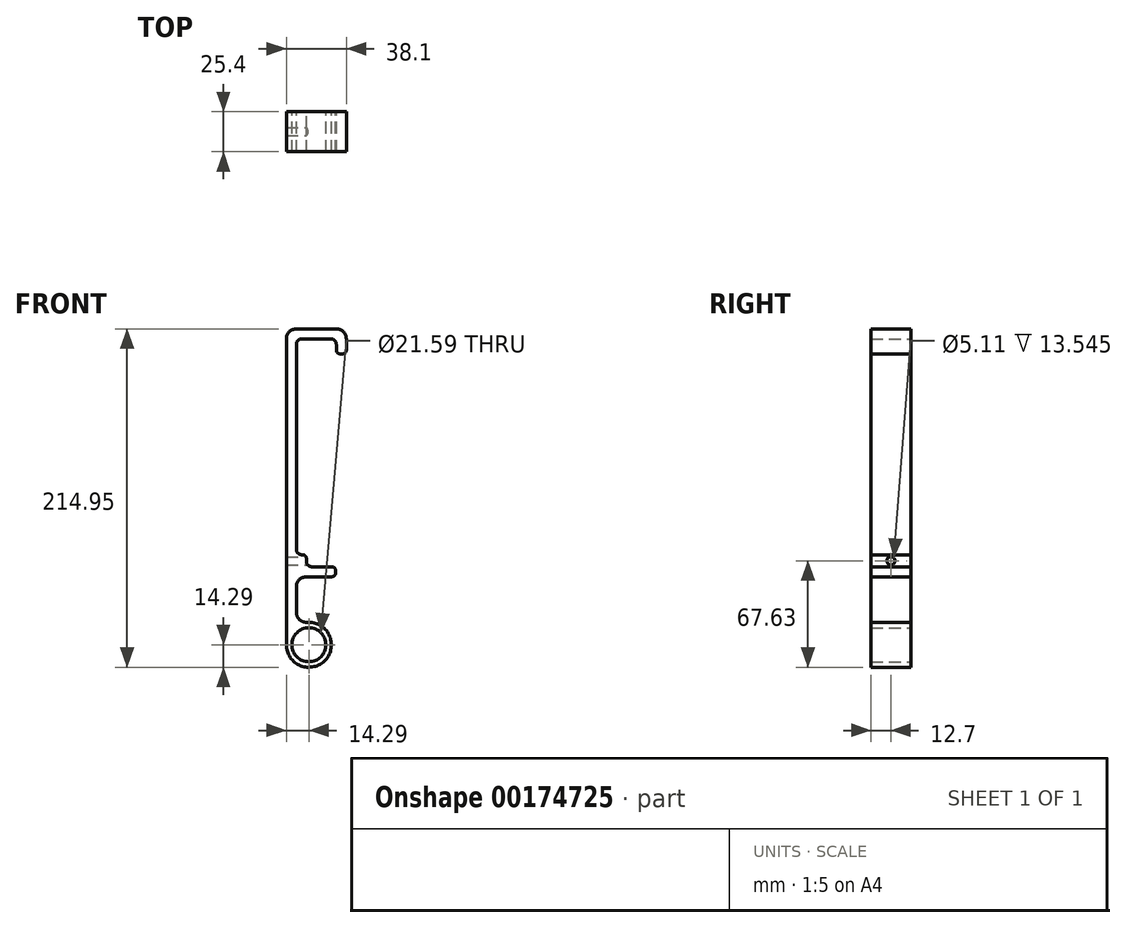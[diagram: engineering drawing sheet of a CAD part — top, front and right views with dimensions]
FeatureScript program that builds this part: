
annotation { "Feature Type Name" : "Feature", "Feature Type Description" : "" }
export const myFeature = defineFeature(function(context is Context, id is Id, definition is map)
    precondition{}
    {
        {
            var Q0;
            Q0=qCreatedBy(makeId("Front.planeOp"),FACE);
            var sketch = newSketch(context, id + "F0", { "sketchPlane" : qUnion([Q0])});
            skCircle(sketch, "E0", {"center": v(0, 0) * mm, "radius": 10.8 * mm});
            skArc(sketch, "E1", {"start": v(-14.29, 0) * mm, "mid": v(12.6, -6.74) * mm, "end": v(-7.94, 11.88) * mm});
            skLineSegment(sketch, "E2", {"start": v(-14.29, 0) * mm, "end": v(-14.29, 200.66) * mm});
            skLineSegment(sketch, "E3", {"start": v(23.81, 200.66) * mm, "end": v(23.81, 184.79) * mm});
            skLineSegment(sketch, "E4", {"start": v(23.81, 184.79) * mm, "end": v(17.46, 184.79) * mm});
            skLineSegment(sketch, "E5", {"start": v(17.46, 184.79) * mm, "end": v(17.46, 194.31) * mm});
            skLineSegment(sketch, "E6", {"start": v(17.46, 194.31) * mm, "end": v(-7.94, 194.31) * mm});
            skLineSegment(sketch, "E7", {"start": v(-7.94, 194.31) * mm, "end": v(-7.94, 57.15) * mm});
            skLineSegment(sketch, "E8", {"start": v(-14.29, 200.66) * mm, "end": v(23.81, 200.66) * mm});
            skLineSegment(sketch, "E9", {"start": v(-1.59, 49.53) * mm, "end": v(16.95, 49.53) * mm});
            skLineSegment(sketch, "E10", {"start": v(16.95, 49.53) * mm, "end": v(16.95, 43.18) * mm});
            skLineSegment(sketch, "E11", {"start": v(16.95, 43.18) * mm, "end": v(-7.94, 43.18) * mm});
            skLineSegment(sketch, "E12.trimOffspring", {"start": v(-7.94, 43.18) * mm, "end": v(-7.94, 11.88) * mm});
            skLineSegment(sketch, "E13", {"start": v(-1.59, 49.53) * mm, "end": v(-1.59, 57.15) * mm});
            skLineSegment(sketch, "E14", {"start": v(-1.59, 57.15) * mm, "end": v(-7.94, 57.15) * mm});
            skSolve(sketch);
        }
        {
            var Q0;
            Q0 = qSketchRegion(id + "F0", true);
            extrude(context, id + "F1", {"entities" : qUnion([Q0]), "depth" : 25.4 * mm});
        }
        {
            var Q0;
            Q0=makeQuery(id+"F1.opExtrude","SWEPT_EDGE",EDGE,{"disambiguationData":[OSD([sQuery(id+"F0.wireOp",EDGE,"E10"),sQuery(id+"F0.wireOp",EDGE,"E11")])]});
            var Q1;
            Q1=makeQuery(id+"F1.opExtrude","SWEPT_EDGE",EDGE,{"disambiguationData":[OSD([sQuery(id+"F0.wireOp",EDGE,"E9"),sQuery(id+"F0.wireOp",EDGE,"E10")])]});
            var Q2;
            Q2=makeQuery(id+"F1.opExtrude","SWEPT_EDGE",EDGE,{"disambiguationData":[OSD([sQuery(id+"F0.wireOp",EDGE,"E3"),sQuery(id+"F0.wireOp",EDGE,"E4")])]});
            var Q3;
            Q3=makeQuery(id+"F1.opExtrude","SWEPT_EDGE",EDGE,{"disambiguationData":[OSD([sQuery(id+"F0.wireOp",EDGE,"E4"),sQuery(id+"F0.wireOp",EDGE,"E5")])]});
            var Q4;
            Q4=makeQuery(id+"F1.opExtrude","SWEPT_EDGE",EDGE,{"disambiguationData":[OSD([sQuery(id+"F0.wireOp",EDGE,"E13"),sQuery(id+"F0.wireOp",EDGE,"E14")])]});
            fillet(context, id + "F2", {"entities" : qUnion([Q0, Q1, Q2, Q3, Q4]), "radius" : 2.3 * mm, "tangentPropagation" : true, "allowEdgeOverflow" : false});
        }
        {
            var Q0;
            Q0=makeQuery(id+"F1.opExtrude","SWEPT_EDGE",EDGE,{"disambiguationData":[OSD([sQuery(id+"F0.wireOp",EDGE,"E5"),sQuery(id+"F0.wireOp",EDGE,"E6")])]});
            var Q1;
            Q1=makeQuery(id+"F1.opExtrude","SWEPT_EDGE",EDGE,{"disambiguationData":[OSD([sQuery(id+"F0.wireOp",EDGE,"E6"),sQuery(id+"F0.wireOp",EDGE,"E7")])]});
            var Q2;
            Q2=makeQuery(id+"F1.opExtrude","SWEPT_EDGE",EDGE,{"disambiguationData":[OSD([sQuery(id+"F0.wireOp",EDGE,"E7"),sQuery(id+"F0.wireOp",EDGE,"E14")])]});
            var Q3;
            Q3=makeQuery(id+"F1.opExtrude","SWEPT_EDGE",EDGE,{"disambiguationData":[OSD([sQuery(id+"F0.wireOp",EDGE,"E9"),sQuery(id+"F0.wireOp",EDGE,"E13")])]});
            fillet(context, id + "F3", {"entities" : qUnion([Q0, Q1, Q2, Q3]), "radius" : 3.56 * mm, "tangentPropagation" : true, "allowEdgeOverflow" : false});
        }
        {
            var Q0;
            Q0=makeQuery(id+"F1.opExtrude","SWEPT_EDGE",EDGE,{"disambiguationData":[OSD([sQuery(id+"F0.wireOp",EDGE,"E11"),sQuery(id+"F0.wireOp",EDGE,"E12.trimOffspring")])]});
            var Q1;
            Q1=makeQuery(id+"F1.opExtrude","SWEPT_EDGE",EDGE,{"disambiguationData":[OSD([sQuery(id+"F0.wireOp",EDGE,"E3"),sQuery(id+"F0.wireOp",EDGE,"E8")])]});
            var Q2;
            Q2=makeQuery(id+"F1.opExtrude","SWEPT_EDGE",EDGE,{"disambiguationData":[OSD([sQuery(id+"F0.wireOp",EDGE,"E2"),sQuery(id+"F0.wireOp",EDGE,"E8")])]});
            var Q3;
            Q3=makeQuery(id+"F1.opExtrude","SWEPT_EDGE",EDGE,{"disambiguationData":[OSD([sQuery(id+"F0.wireOp",EDGE,"E1"),sQuery(id+"F0.wireOp",EDGE,"E12.trimOffspring")])]});
            fillet(context, id + "F4", {"entities" : qUnion([Q0, Q1, Q2, Q3]), "radius" : 6.35 * mm, "tangentPropagation" : true, "allowEdgeOverflow" : false});
        }
        {
            var Q0;
            Q0=makeQuery(id+"F1.opExtrude","SWEPT_FACE",FACE,{"disambiguationData":[OSD([sQuery(id+"F0.wireOp",EDGE,"E7")])]});
            var sketch = newSketch(context, id + "F5", { "sketchPlane" : qUnion([Q0])});
            skCircle(sketch, "E15", {"center": v(-12.7, 53.34) * mm, "radius": 2.55 * mm});
            skSolve(sketch);
        }
        {
            var Q0;
            Q0 = qSketchRegion(id + "F5", true);
            extrude(context, id + "F6", {"entities" : qUnion([Q0]), "operationType" : NewBodyOperationType.REMOVE, "endBound" : BoundingType.SYMMETRIC, "oppositeDirection" : true, "depth" : 25.4 * mm});
        }
    });
